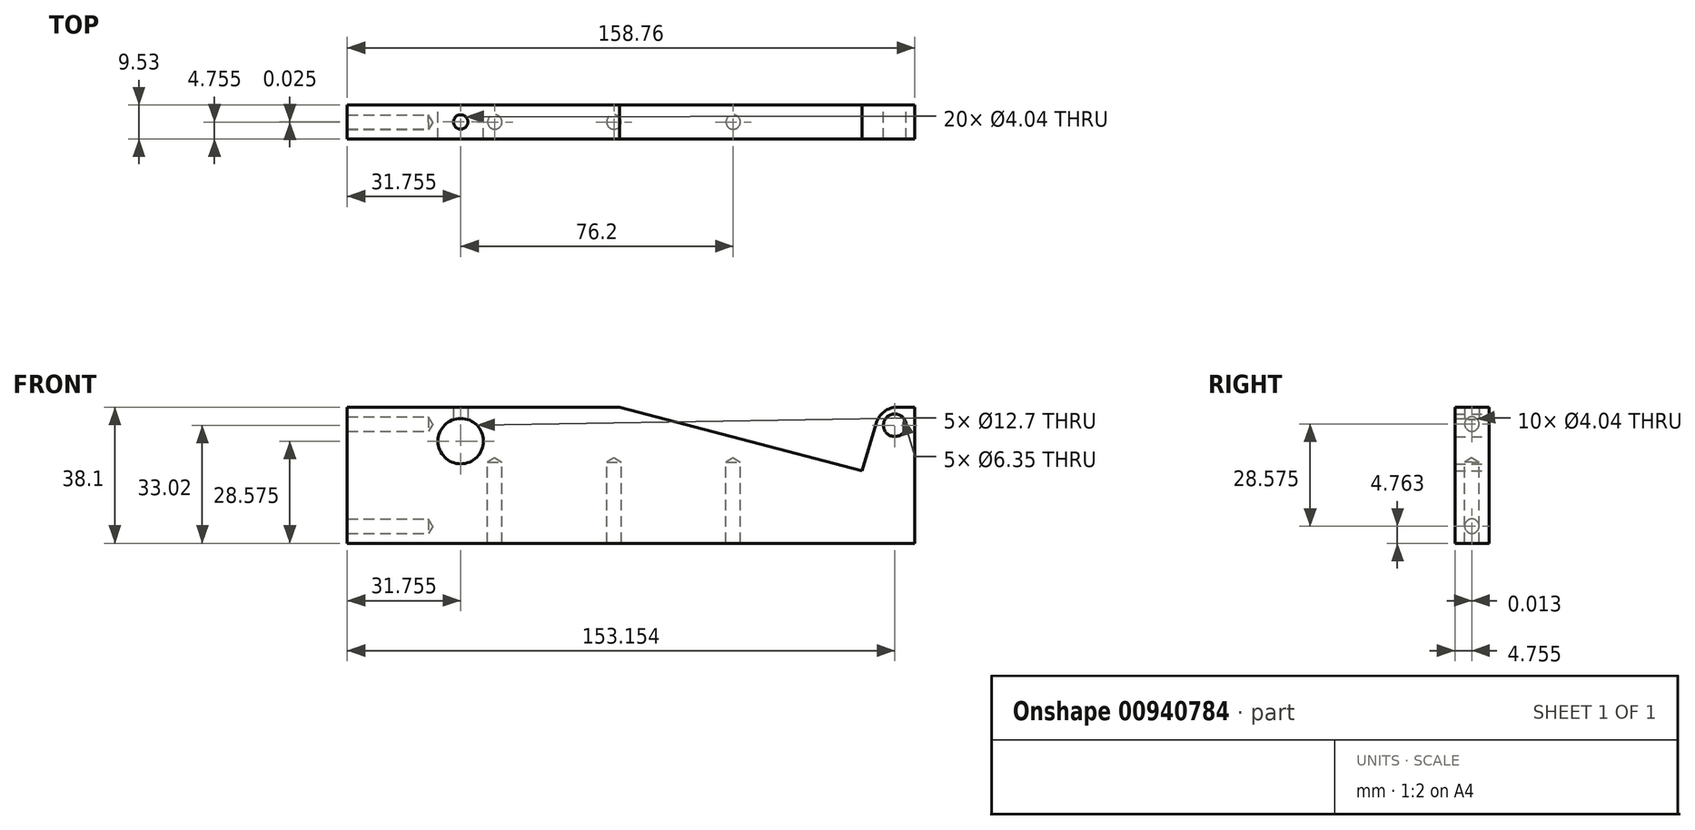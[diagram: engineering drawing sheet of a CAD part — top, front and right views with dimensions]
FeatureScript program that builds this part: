
annotation { "Feature Type Name" : "Feature", "Feature Type Description" : "" }
export const myFeature = defineFeature(function(context is Context, id is Id, definition is map)
    precondition{}
    {
        {
            var Q0;
            Q0=qCreatedBy(makeId("Front.planeOp"),FACE);
            var sketch = newSketch(context, id + "F0", { "sketchPlane" : qUnion([Q0])});
            skLineSegment(sketch, "E0.bottom", {"start": v(-79.38, 19.05) * mm, "end": v(-3.17, 19.05) * mm});
            skLineSegment(sketch, "E0.top", {"start": v(-79.38, -19.05) * mm, "end": v(79.38, -19.05) * mm});
            skLineSegment(sketch, "E0.left", {"start": v(-79.38, 19.05) * mm, "end": v(-79.38, -19.05) * mm});
            skLineSegment(sketch, "E0.right", {"start": v(79.38, 19.05) * mm, "end": v(79.38, -19.05) * mm});
            skPoint(sketch, "E0.middle", {"position": v(0, 0) * mm});
            skCircle(sketch, "E1", {"center": v(-47.62, 9.53) * mm, "radius": 6.35 * mm});
            skCircle(sketch, "E2", {"center": v(73.77, 13.97) * mm, "radius": 3.18 * mm});
            skLineSegment(sketch, "E3", {"start": v(74.6, 19.05) * mm, "end": v(79.38, 19.05) * mm});
            skPoint(sketch, "E4", {"position": v(74.17, 1.27) * mm});
            skPoint(sketch, "E5", {"position": v(64.64, 1.27) * mm});
            skLineSegment(sketch, "E6", {"start": v(68.51, 14.48) * mm, "end": v(64.64, 1.27) * mm});
            skLineSegment(sketch, "E7", {"start": v(-3.17, 19.05) * mm, "end": v(64.64, 1.27) * mm});
            skPoint(sketch, "E8.endSnap0", {"position": v(79.38, 0) * mm});
            skPoint(sketch, "E9.visualSharp", {"position": v(69.85, 19.05) * mm});
            skArc(sketch, "E9.filletArc", {"start": v(74.6, 19.05) * mm, "mid": v(70.8, 17.78) * mm, "end": v(68.51, 14.48) * mm});
            skSolve(sketch);
        }
        {
            var Q0;
            Q0=makeQuery(id+"F0.imprint","IMPRINT",FACE,{"disambiguationData":[TD([[makeQuery(id+"F0.imprint","IMPRINT",EDGE,{"derivedFrom":sQuery(id+"F0.wireOp",EDGE,"E0.bottom")}),-1.0]])]});
            extrude(context, id + "F1", {"entities" : qUnion([Q0]), "depth" : 9.52 * mm, "offsetDistance" : 25.4 * mm});
        }
        {
            var Q0;
            Q0=makeQuery(id+"F1.opExtrude","SWEPT_FACE",FACE,{"disambiguationData":[OSD([sQuery(id+"F0.wireOp",EDGE,"E0.left")])]});
            var sketch = newSketch(context, id + "F2", { "sketchPlane" : qUnion([Q0])});
            skPoint(sketch, "E10", {"position": v(4.76, 14.29) * mm});
            skPoint(sketch, "E11", {"position": v(4.78, -14.29) * mm});
            skSolve(sketch);
        }
        {
            var Q0;
            Q0=sQuery(id+"F2.wireOp",VERTEX,"E10");
            var Q1;
            Q1=sQuery(id+"F2.wireOp",VERTEX,"E11");
            var Q2;
            Q2=makeQuery(id+"F1.opExtrude","SWEPT_BODY",BODY,{"disambiguationData":[OSD([sQuery(id+"F0.wireOp",EDGE,"E0.bottom"),sQuery(id+"F0.wireOp",EDGE,"E0.top"),sQuery(id+"F0.wireOp",EDGE,"E0.left"),sQuery(id+"F0.wireOp",EDGE,"E0.right"),sQuery(id+"F0.wireOp",EDGE,"E1"),sQuery(id+"F0.wireOp",EDGE,"E2"),sQuery(id+"F0.wireOp",EDGE,"qVi7euF6-7O9x-nSrJ-l2Mr-fCC4ulKBCPIk"),sQuery(id+"F0.wireOp",EDGE,"9X8vyIEC-xuGj-BpOn-BGC1-W7P4dCBtnZX7"),sQuery(id+"F0.wireOp",EDGE,"E3")])]});
            hole(context, id + "F3", {"style" : HoleStyle.SIMPLE, "endStyle" : HoleEndStyle.BLIND, "standardTappedOrClearance" : lookupTablePath({ "standard" : "ANSI", "engagement" : "75%", "pitch" : "32 tpi", "size" : "#10", "type" : "Tapped" }), "standardBlindInLast" : lookupTablePath({ "standard" : "ANSI", "engagement" : "75%", "pitch" : "32 tpi", "size" : "#10", "type" : "Tapped" }), "holeDiameter" : 4.04 * mm, "showTappedDepth" : true, "holeDepth" : 22.7 * mm, "tappedDepth" : 20.32 * mm, "tapClearance" : 3, "locations" : qUnion([Q0, Q1]), "scope" : qUnion([Q2]), "majorDiameter" : 4.83 * mm});
        }
        {
            var Q0;
            Q0=makeQuery(id+"F1.opExtrude","SWEPT_FACE",FACE,{"disambiguationData":[OSD([sQuery(id+"F0.wireOp",EDGE,"E0.bottom")])]});
            var sketch = newSketch(context, id + "F4", { "sketchPlane" : qUnion([Q0])});
            skPoint(sketch, "E12", {"position": v(-47.62, -4.75) * mm});
            skSolve(sketch);
        }
        {
            var Q0;
            Q0=sQuery(id+"F4.wireOp",VERTEX,"E12");
            var Q1;
            Q1=makeQuery(id+"F1.opExtrude","SWEPT_BODY",BODY,{"disambiguationData":[OSD([sQuery(id+"F0.wireOp",EDGE,"E0.bottom"),sQuery(id+"F0.wireOp",EDGE,"E0.top"),sQuery(id+"F0.wireOp",EDGE,"E0.left"),sQuery(id+"F0.wireOp",EDGE,"E0.right"),sQuery(id+"F0.wireOp",EDGE,"E1"),sQuery(id+"F0.wireOp",EDGE,"E2"),sQuery(id+"F0.wireOp",EDGE,"qVi7euF6-7O9x-nSrJ-l2Mr-fCC4ulKBCPIk"),sQuery(id+"F0.wireOp",EDGE,"9X8vyIEC-xuGj-BpOn-BGC1-W7P4dCBtnZX7"),sQuery(id+"F0.wireOp",EDGE,"E3")])]});
            hole(context, id + "F5", {"style" : HoleStyle.SIMPLE, "endStyle" : HoleEndStyle.BLIND, "standardTappedOrClearance" : lookupTablePath({ "standard" : "ANSI", "engagement" : "75%", "pitch" : "32 tpi", "size" : "#10", "type" : "Tapped" }), "standardBlindInLast" : lookupTablePath({ "standard" : "ANSI", "engagement" : "75%", "pitch" : "32 tpi", "size" : "#10", "type" : "Tapped" }), "holeDiameter" : 4.04 * mm, "showTappedDepth" : true, "holeDepth" : 11.9 * mm, "tappedDepth" : 9.52 * mm, "tapClearance" : 3, "locations" : qUnion([Q0]), "scope" : qUnion([Q1]), "majorDiameter" : 4.83 * mm});
        }
        {
            var Q0;
            Q0=makeQuery(id+"F1.opExtrude","SWEPT_FACE",FACE,{"disambiguationData":[OSD([sQuery(id+"F0.wireOp",EDGE,"E0.top")])]});
            var sketch = newSketch(context, id + "F6", { "sketchPlane" : qUnion([Q0])});
            skPoint(sketch, "E13", {"position": v(28.58, 4.78) * mm});
            skPoint(sketch, "E14", {"position": v(-38.1, 4.76) * mm});
            skPoint(sketch, "E15", {"position": v(-4.76, 4.78) * mm});
            skSolve(sketch);
        }
        {
            var Q0;
            Q0=sQuery(id+"F6.wireOp",VERTEX,"E14");
            var Q1;
            Q1=sQuery(id+"F6.wireOp",VERTEX,"E15");
            var Q2;
            Q2=sQuery(id+"F6.wireOp",VERTEX,"E13");
            var Q3;
            Q3=makeQuery(id+"F1.opExtrude","SWEPT_BODY",BODY,{"disambiguationData":[OSD([sQuery(id+"F0.wireOp",EDGE,"E0.bottom"),sQuery(id+"F0.wireOp",EDGE,"E0.top"),sQuery(id+"F0.wireOp",EDGE,"E0.left"),sQuery(id+"F0.wireOp",EDGE,"E0.right"),sQuery(id+"F0.wireOp",EDGE,"E1"),sQuery(id+"F0.wireOp",EDGE,"E2"),sQuery(id+"F0.wireOp",EDGE,"qVi7euF6-7O9x-nSrJ-l2Mr-fCC4ulKBCPIk"),sQuery(id+"F0.wireOp",EDGE,"9X8vyIEC-xuGj-BpOn-BGC1-W7P4dCBtnZX7"),sQuery(id+"F0.wireOp",EDGE,"E3")])]});
            hole(context, id + "F7", {"style" : HoleStyle.SIMPLE, "endStyle" : HoleEndStyle.BLIND, "standardTappedOrClearance" : lookupTablePath({ "standard" : "ANSI", "engagement" : "75%", "pitch" : "32 tpi", "size" : "#10", "type" : "Tapped" }), "standardBlindInLast" : lookupTablePath({ "standard" : "ANSI", "engagement" : "75%", "pitch" : "32 tpi", "size" : "#10", "type" : "Tapped" }), "holeDiameter" : 4.04 * mm, "showTappedDepth" : true, "holeDepth" : 22.7 * mm, "tappedDepth" : 20.33 * mm, "tapClearance" : 3, "locations" : qUnion([Q0, Q1, Q2]), "scope" : qUnion([Q3]), "majorDiameter" : 4.83 * mm});
        }
    });
